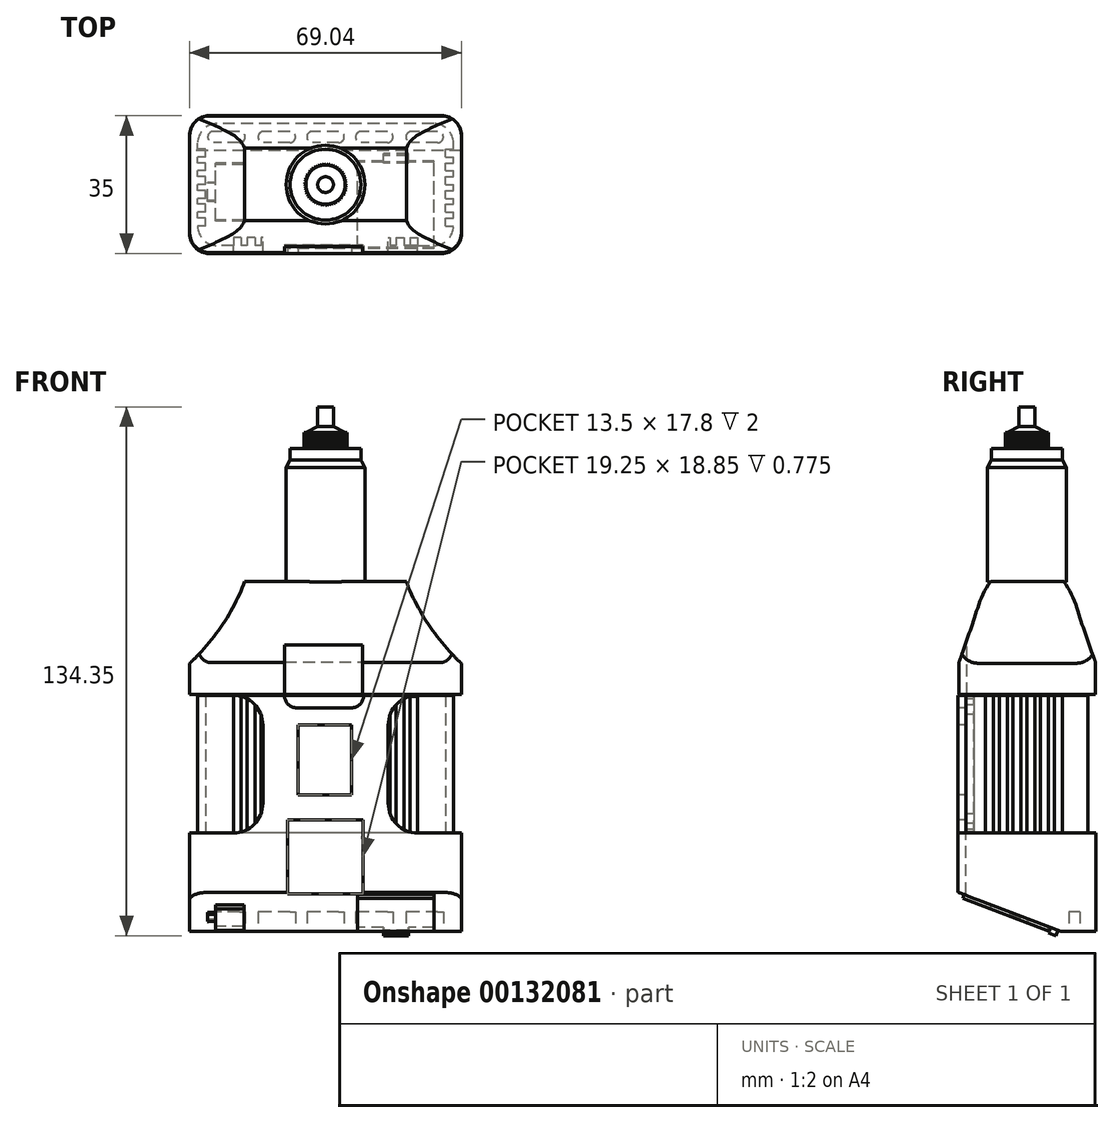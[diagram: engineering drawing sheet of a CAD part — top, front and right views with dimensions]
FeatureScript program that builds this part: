
annotation { "Feature Type Name" : "Feature", "Feature Type Description" : "" }
export const myFeature = defineFeature(function(context is Context, id is Id, definition is map)
    precondition{}
    {
        {
            var Q0;
            Q0=qCreatedBy(makeId("Front.planeOp"),FACE);
            var sketch = newSketch(context, id + "F0", { "sketchPlane" : qUnion([Q0])});
            skLineSegment(sketch, "E0.bottom", {"start": v(32.52, 25.25) * mm, "end": v(-32.53, 25.25) * mm});
            skLineSegment(sketch, "E0.top", {"start": v(32.53, -25.25) * mm, "end": v(-32.52, -25.25) * mm});
            skLineSegment(sketch, "E0.left", {"start": v(32.52, 25.25) * mm, "end": v(32.53, -25.25) * mm});
            skLineSegment(sketch, "E0.right", {"start": v(-32.53, 25.25) * mm, "end": v(-32.52, -25.25) * mm});
            skPoint(sketch, "E0.middle", {"position": v(0, 0) * mm});
            skSolve(sketch);
        }
        {
            var Q0;
            Q0=makeQuery(id+"F0.imprint","IMPRINT",FACE,{"disambiguationData":[TD([[makeQuery(id+"F0.imprint","IMPRINT",EDGE,{"derivedFrom":sQuery(id+"F0.wireOp",EDGE,"E0.bottom")}),1.0]])]});
            extrude(context, id + "F1", {"entities" : qUnion([Q0]), "endBound" : BoundingType.SYMMETRIC, "depth" : 31 * mm});
        }
        {
            var Q0;
            Q0=makeQuery(id+"F1.opExtrude","CAP_FACE",FACE,{"disambiguationData":[OSD([sQuery(id+"F0.wireOp",EDGE,"E0.bottom"),sQuery(id+"F0.wireOp",EDGE,"E0.top"),sQuery(id+"F0.wireOp",EDGE,"E0.left"),sQuery(id+"F0.wireOp",EDGE,"E0.right")])],"isStart":false});
            var sketch = newSketch(context, id + "F2", { "sketchPlane" : qUnion([Q0])});
            skLineSegment(sketch, "E1", {"start": v(-32.52, -9.75) * mm, "end": v(-23.43, -9.75) * mm});
            skLineSegment(sketch, "E2", {"start": v(-32.52, -25.25) * mm, "end": v(32.53, -25.25) * mm});
            skLineSegment(sketch, "E3", {"start": v(-15.93, 17.75) * mm, "end": v(-15.92, -2.25) * mm});
            skLineSegment(sketch, "E4", {"start": v(15.92, 17.75) * mm, "end": v(15.92, -2.25) * mm});
            skLineSegment(sketch, "E5", {"start": v(-32.52, -9.75) * mm, "end": v(-32.52, -25.25) * mm});
            skLineSegment(sketch, "E6", {"start": v(32.53, -9.75) * mm, "end": v(32.53, -25.25) * mm});
            skLineSegment(sketch, "E7.trimOffspring", {"start": v(23.43, -9.75) * mm, "end": v(32.53, -9.75) * mm});
            skArc(sketch, "E8", {"start": v(-23.43, -9.75) * mm, "mid": v(-18.12, -7.55) * mm, "end": v(-15.92, -2.25) * mm});
            skArc(sketch, "E9", {"start": v(15.92, -2.25) * mm, "mid": v(18.12, -7.55) * mm, "end": v(23.43, -9.75) * mm});
            skPoint(sketch, "E10.orphan", {"position": v(-15.93, 25.25) * mm});
            skPoint(sketch, "E11.start.orphan", {"position": v(-23.43, 25.25) * mm});
            skArc(sketch, "E12", {"start": v(-15.93, 17.75) * mm, "mid": v(-18.12, 23.05) * mm, "end": v(-23.43, 25.25) * mm});
            skPoint(sketch, "E13.orphan", {"position": v(15.92, 25.25) * mm});
            skPoint(sketch, "E14.trimOffspring.end.orphan", {"position": v(32.52, 17.75) * mm});
            skLineSegment(sketch, "E15.trimOffspring", {"start": v(15.92, 25.25) * mm, "end": v(-15.93, 25.25) * mm});
            skPoint(sketch, "E16.trimOffspring.end.orphan", {"position": v(32.53, -2.25) * mm});
            skArc(sketch, "E17", {"start": v(23.42, 25.25) * mm, "mid": v(18.12, 23.05) * mm, "end": v(15.92, 17.75) * mm});
            skLineSegment(sketch, "E18", {"start": v(-23.43, 25.25) * mm, "end": v(-15.93, 25.25) * mm});
            skLineSegment(sketch, "E19", {"start": v(15.92, 25.25) * mm, "end": v(23.42, 25.25) * mm});
            skPoint(sketch, "E20.start.orphan", {"position": v(32.52, 25.25) * mm});
            skSolve(sketch);
        }
        {
            var Q0;
            Q0 = qSketchRegion(id + "F2", true);
            extrude(context, id + "F3", {"entities" : qUnion([Q0]), "operationType" : NewBodyOperationType.ADD, "depth" : 2 * mm});
        }
        {
            var Q0;
            Q0=makeQuery(id+"F3.opExtrude","CAP_FACE",FACE,{"disambiguationData":[OSD([sQuery(id+"F2.wireOp",EDGE,"E1"),sQuery(id+"F2.wireOp",EDGE,"E2"),sQuery(id+"F2.wireOp",EDGE,"E3"),sQuery(id+"F2.wireOp",EDGE,"E4"),sQuery(id+"F2.wireOp",EDGE,"E5"),sQuery(id+"F2.wireOp",EDGE,"E6"),sQuery(id+"F2.wireOp",EDGE,"E7.trimOffspring"),sQuery(id+"F2.wireOp",EDGE,"E8"),sQuery(id+"F2.wireOp",EDGE,"E9"),sQuery(id+"F2.wireOp",EDGE,"E12"),sQuery(id+"F2.wireOp",EDGE,"E15.trimOffspring"),sQuery(id+"F2.wireOp",EDGE,"E17"),sQuery(id+"F2.wireOp",EDGE,"E18"),sQuery(id+"F2.wireOp",EDGE,"E19")])],"isStart":false});
            var sketch = newSketch(context, id + "F4", { "sketchPlane" : qUnion([Q0])});
            skLineSegment(sketch, "E21", {"start": v(-15.93, 17.75) * mm, "end": v(15.92, 17.75) * mm, "construction": true});
            skLineSegment(sketch, "E22.bottom", {"start": v(-6.93, 17.75) * mm, "end": v(6.57, 17.75) * mm});
            skLineSegment(sketch, "E22.top", {"start": v(-6.93, -0.05) * mm, "end": v(6.57, -0.05) * mm});
            skLineSegment(sketch, "E22.left", {"start": v(-6.93, 17.75) * mm, "end": v(-6.93, -0.05) * mm});
            skLineSegment(sketch, "E22.right", {"start": v(6.57, 17.75) * mm, "end": v(6.57, -0.05) * mm});
            skLineSegment(sketch, "E23", {"start": v(-7.26, 22.05) * mm, "end": v(6.5, 22.05) * mm});
            skPoint(sketch, "E24.start.orphan", {"position": v(9.39, 25.25) * mm});
            skArc(sketch, "E25", {"start": v(6.5, 22.05) * mm, "mid": v(8.76, 22.99) * mm, "end": v(9.7, 25.25) * mm});
            skPoint(sketch, "E26.orphan", {"position": v(-10.85, 25.25) * mm});
            skArc(sketch, "E27", {"start": v(-7.26, 22.05) * mm, "mid": v(-9.52, 22.99) * mm, "end": v(-10.46, 25.25) * mm});
            skLineSegment(sketch, "E28", {"start": v(-9.7, -25.25) * mm, "end": v(-9.7, -6.4) * mm});
            skLineSegment(sketch, "E29", {"start": v(-9.7, -6.4) * mm, "end": v(9.56, -6.4) * mm});
            skLineSegment(sketch, "E30", {"start": v(9.56, -6.4) * mm, "end": v(9.56, -25.25) * mm});
            skSolve(sketch);
        }
        {
            var Q0;
            Q0=makeQuery(id+"F3.boolean.opBoolean","MERGE",FACE,{"derivedFrom":[makeQuery(id+"F1.opExtrude","SWEPT_FACE",FACE,{"disambiguationData":[OSD([sQuery(id+"F0.wireOp",EDGE,"E0.top")])]}),makeQuery(id+"F3.opExtrude","SWEPT_FACE",FACE,{"disambiguationData":[OSD([sQuery(id+"F2.wireOp",EDGE,"E2")])]})]});
            var sketch = newSketch(context, id + "F5", { "sketchPlane" : qUnion([Q0])});
            skLineSegment(sketch, "E31.bottom", {"start": v(-32.52, 17.5) * mm, "end": v(32.53, 17.5) * mm});
            skLineSegment(sketch, "E31.top", {"start": v(-32.52, -15.5) * mm, "end": v(32.53, -15.5) * mm});
            skLineSegment(sketch, "E31.left", {"start": v(-32.52, 17.5) * mm, "end": v(-32.52, -15.5) * mm});
            skLineSegment(sketch, "E31.right", {"start": v(32.53, 17.5) * mm, "end": v(32.53, -15.5) * mm});
            skSolve(sketch);
        }
        {
            var Q0;
            Q0 = qSketchRegion(id + "F5", true);
            extrude(context, id + "F6", {"entities" : qUnion([Q0]), "operationType" : NewBodyOperationType.ADD, "depth" : 9.5 * mm});
        }
        {
            var Q0;
            Q0=makeQuery(id+"F6.boolean.opBoolean","MERGE",FACE,{"derivedFrom":[makeQuery(id+"F3.boolean.opBoolean","MERGE",FACE,{"derivedFrom":[makeQuery(id+"F1.opExtrude","SWEPT_FACE",FACE,{"disambiguationData":[OSD([sQuery(id+"F0.wireOp",EDGE,"E0.right")])]}),makeQuery(id+"F3.opExtrude","SWEPT_FACE",FACE,{"disambiguationData":[OSD([sQuery(id+"F2.wireOp",EDGE,"E5")])]})]}),makeQuery(id+"F6.opExtrude","SWEPT_FACE",FACE,{"disambiguationData":[OSD([sQuery(id+"F5.wireOp",EDGE,"E31.left")])]})]});
            var sketch = newSketch(context, id + "F7", { "sketchPlane" : qUnion([Q0])});
            skLineSegment(sketch, "E32", {"start": v(-8.68, -34.75) * mm, "end": v(17.5, -24.78) * mm});
            skLineSegment(sketch, "E33", {"start": v(17.5, -24.78) * mm, "end": v(17.5, -34.75) * mm});
            skLineSegment(sketch, "E34", {"start": v(17.5, -34.75) * mm, "end": v(-8.68, -34.75) * mm});
            skSolve(sketch);
        }
        {
            var Q0;
            Q0 = qSketchRegion(id + "F7", true);
            extrude(context, id + "F8", {"entities" : qUnion([Q0]), "operationType" : NewBodyOperationType.REMOVE, "endBound" : BoundingType.THROUGH_ALL, "oppositeDirection" : true, "depth" : 25 * mm});
        }
        {
            var Q0;
            Q0 = qSketchRegion(id + "F4", true);
            extrude(context, id + "F9", {"entities" : qUnion([Q0]), "operationType" : NewBodyOperationType.REMOVE, "oppositeDirection" : true, "depth" : 2 * mm});
        }
        {
            var Q0;
            {var subQ0=sQuery(id+"F4.wireOp",EDGE,"E28");Q0=makeQuery(id+"F4.imprint","IMPRINT",FACE,{"disambiguationData":[TD([[makeQuery(id+"F4.imprint","IMPRINT",EDGE,{"derivedFrom":subQ0}),-1.0]])]});}
            extrude(context, id + "F10", {"entities" : qUnion([Q0]), "operationType" : NewBodyOperationType.REMOVE, "oppositeDirection" : true, "depth" : 2 * mm});
        }
        {
            var Q0;
            Q0=makeQuery(id+"F4.imprint","IMPRINT",FACE,{"disambiguationData":[TD([[makeQuery(id+"F4.imprint","IMPRINT",EDGE,{"derivedFrom":sQuery(id+"F4.wireOp",EDGE,"E23")}),1.0]])]});
            extrude(context, id + "F11", {"entities" : qUnion([Q0]), "operationType" : NewBodyOperationType.REMOVE, "oppositeDirection" : true, "depth" : 2 * mm});
        }
        {
            var Q0;
            Q0=makeQuery(id+"F6.opExtrude","CAP_FACE",FACE,{"disambiguationData":[OSD([sQuery(id+"F5.wireOp",EDGE,"E31.bottom"),sQuery(id+"F5.wireOp",EDGE,"E31.top"),sQuery(id+"F5.wireOp",EDGE,"E31.left"),sQuery(id+"F5.wireOp",EDGE,"E31.right")])],"isStart":false});
            var sketch = newSketch(context, id + "F12", { "sketchPlane" : qUnion([Q0])});
            skLineSegment(sketch, "E35.bottom", {"start": v(-21.85, -10.66) * mm, "end": v(-28.5, -10.66) * mm});
            skLineSegment(sketch, "E35.top", {"start": v(-21.85, -13.51) * mm, "end": v(-28.5, -13.51) * mm});
            skPoint(sketch, "E35.middle", {"position": v(-25.17, -12.1) * mm});
            skLineSegment(sketch, "E36.bottom", {"start": v(-9.07, -10.66) * mm, "end": v(-15.71, -10.66) * mm});
            skLineSegment(sketch, "E36.top", {"start": v(-9.07, -13.52) * mm, "end": v(-15.71, -13.52) * mm});
            skPoint(sketch, "E36.middle", {"position": v(-12.39, -12.09) * mm});
            skLineSegment(sketch, "E37.bottom", {"start": v(3.32, -10.66) * mm, "end": v(-3.32, -10.66) * mm});
            skLineSegment(sketch, "E37.top", {"start": v(3.33, -13.52) * mm, "end": v(-3.32, -13.52) * mm});
            skPoint(sketch, "E37.middle", {"position": v(0, -12.1) * mm});
            skLineSegment(sketch, "E38.bottom", {"start": v(15.71, -10.67) * mm, "end": v(9.06, -10.67) * mm});
            skLineSegment(sketch, "E38.top", {"start": v(15.71, -13.51) * mm, "end": v(9.06, -13.51) * mm});
            skPoint(sketch, "E38.middle", {"position": v(12.39, -12.09) * mm});
            skLineSegment(sketch, "E39.bottom", {"start": v(28.5, -10.66) * mm, "end": v(21.85, -10.66) * mm});
            skLineSegment(sketch, "E39.top", {"start": v(28.5, -13.51) * mm, "end": v(21.85, -13.51) * mm});
            skPoint(sketch, "E39.middle", {"position": v(25.18, -12.09) * mm});
            skArc(sketch, "E40", {"start": v(-28.5, -10.66) * mm, "mid": v(-29.92, -12.09) * mm, "end": v(-28.5, -13.51) * mm});
            skArc(sketch, "E41", {"start": v(-21.85, -10.67) * mm, "mid": v(-20.42, -12.1) * mm, "end": v(-21.85, -13.51) * mm});
            skArc(sketch, "E42", {"start": v(28.5, -10.66) * mm, "mid": v(29.93, -12.09) * mm, "end": v(28.5, -13.51) * mm});
            skArc(sketch, "E43", {"start": v(21.85, -10.66) * mm, "mid": v(20.43, -12.09) * mm, "end": v(21.85, -13.51) * mm});
            skArc(sketch, "E44", {"start": v(-3.33, -13.52) * mm, "mid": v(-4.75, -12.1) * mm, "end": v(-3.32, -10.66) * mm});
            skArc(sketch, "E45", {"start": v(3.32, -10.67) * mm, "mid": v(4.75, -12.1) * mm, "end": v(3.33, -13.52) * mm});
            skArc(sketch, "E46", {"start": v(-9.07, -10.66) * mm, "mid": v(-7.64, -12.09) * mm, "end": v(-9.07, -13.52) * mm});
            skArc(sketch, "E47", {"start": v(-15.71, -10.66) * mm, "mid": v(-17.14, -12.09) * mm, "end": v(-15.71, -13.52) * mm});
            skArc(sketch, "E48", {"start": v(15.71, -10.67) * mm, "mid": v(17.14, -12.1) * mm, "end": v(15.71, -13.51) * mm});
            skArc(sketch, "E49", {"start": v(9.06, -10.67) * mm, "mid": v(7.64, -12.1) * mm, "end": v(9.06, -13.51) * mm});
            skSolve(sketch);
        }
        {
            var Q0;
            Q0 = qSketchRegion(id + "F12", true);
            extrude(context, id + "F13", {"entities" : qUnion([Q0]), "operationType" : NewBodyOperationType.REMOVE, "oppositeDirection" : true, "depth" : 5 * mm});
        }
        {
            var Q0;
            Q0=makeQuery(id+"F6.boolean.opBoolean","MERGE",FACE,{"derivedFrom":[makeQuery(id+"F3.boolean.opBoolean","MERGE",FACE,{"derivedFrom":[makeQuery(id+"F1.opExtrude","SWEPT_FACE",FACE,{"disambiguationData":[OSD([sQuery(id+"F0.wireOp",EDGE,"E0.right")])]}),makeQuery(id+"F3.opExtrude","SWEPT_FACE",FACE,{"disambiguationData":[OSD([sQuery(id+"F2.wireOp",EDGE,"E5")])]})]}),makeQuery(id+"F6.opExtrude","SWEPT_FACE",FACE,{"disambiguationData":[OSD([sQuery(id+"F5.wireOp",EDGE,"E31.left")])]})]});
            var sketch = newSketch(context, id + "F14", { "sketchPlane" : qUnion([Q0])});
            skLineSegment(sketch, "E50", {"start": v(17.5, -9.75) * mm, "end": v(-15.5, -9.75) * mm});
            skLineSegment(sketch, "E51", {"start": v(-15.5, -9.75) * mm, "end": v(-15.5, -34.75) * mm});
            skLineSegment(sketch, "E52", {"start": v(-15.5, -34.75) * mm, "end": v(-8.68, -34.75) * mm});
            skLineSegment(sketch, "E53", {"start": v(-8.68, -34.75) * mm, "end": v(17.5, -24.78) * mm});
            skLineSegment(sketch, "E54", {"start": v(17.5, -24.78) * mm, "end": v(17.5, -9.75) * mm});
            skSolve(sketch);
        }
        {
            var Q0;
            Q0 = qSketchRegion(id + "F14", true);
            extrude(context, id + "F15", {"entities" : qUnion([Q0]), "operationType" : NewBodyOperationType.ADD, "depth" : 2 * mm});
        }
        {
            var Q0;
            Q0=makeQuery(id+"F6.boolean.opBoolean","MERGE",FACE,{"derivedFrom":[makeQuery(id+"F3.boolean.opBoolean","MERGE",FACE,{"derivedFrom":[makeQuery(id+"F1.opExtrude","SWEPT_FACE",FACE,{"disambiguationData":[OSD([sQuery(id+"F0.wireOp",EDGE,"E0.left")])]}),makeQuery(id+"F3.opExtrude","SWEPT_FACE",FACE,{"disambiguationData":[OSD([sQuery(id+"F2.wireOp",EDGE,"E6")])]})]}),makeQuery(id+"F6.opExtrude","SWEPT_FACE",FACE,{"disambiguationData":[OSD([sQuery(id+"F5.wireOp",EDGE,"E31.right")])]})]});
            var sketch = newSketch(context, id + "F16", { "sketchPlane" : qUnion([Q0])});
            skLineSegment(sketch, "E55", {"start": v(-17.5, -9.75) * mm, "end": v(15.5, -9.75) * mm});
            skLineSegment(sketch, "E56", {"start": v(15.5, -9.75) * mm, "end": v(15.5, -34.75) * mm});
            skLineSegment(sketch, "E57", {"start": v(15.5, -34.75) * mm, "end": v(8.68, -34.75) * mm});
            skLineSegment(sketch, "E58", {"start": v(8.68, -34.75) * mm, "end": v(-17.5, -24.78) * mm});
            skLineSegment(sketch, "E59", {"start": v(-17.5, -24.78) * mm, "end": v(-17.5, -9.75) * mm});
            skSolve(sketch);
        }
        {
            var Q0;
            Q0 = qSketchRegion(id + "F16", true);
            extrude(context, id + "F17", {"entities" : qUnion([Q0]), "operationType" : NewBodyOperationType.ADD, "depth" : 2 * mm});
        }
        {
            var Q0;
            Q0=makeQuery(id+"F17.boolean.opBoolean","MERGE",FACE,{"derivedFrom":[makeQuery(id+"F15.boolean.opBoolean","MERGE",FACE,{"derivedFrom":[makeQuery(id+"F6.boolean.opBoolean","MERGE",FACE,{"derivedFrom":[makeQuery(id+"F1.opExtrude","CAP_FACE",FACE,{"disambiguationData":[OSD([sQuery(id+"F0.wireOp",EDGE,"E0.bottom"),sQuery(id+"F0.wireOp",EDGE,"E0.top"),sQuery(id+"F0.wireOp",EDGE,"E0.left"),sQuery(id+"F0.wireOp",EDGE,"E0.right")])],"isStart":true}),makeQuery(id+"F6.opExtrude","SWEPT_FACE",FACE,{"disambiguationData":[OSD([sQuery(id+"F5.wireOp",EDGE,"E31.top")])]})]}),makeQuery(id+"F15.opExtrude","SWEPT_FACE",FACE,{"disambiguationData":[OSD([sQuery(id+"F14.wireOp",EDGE,"E51")])]})]}),makeQuery(id+"F17.opExtrude","SWEPT_FACE",FACE,{"disambiguationData":[OSD([sQuery(id+"F16.wireOp",EDGE,"E56")])]})]});
            var sketch = newSketch(context, id + "F18", { "sketchPlane" : qUnion([Q0])});
            skLineSegment(sketch, "E60", {"start": v(-34.53, -9.75) * mm, "end": v(34.52, -9.75) * mm});
            skLineSegment(sketch, "E61", {"start": v(-34.53, -9.75) * mm, "end": v(-34.53, -34.75) * mm});
            skLineSegment(sketch, "E62", {"start": v(-34.53, -34.75) * mm, "end": v(34.52, -34.75) * mm});
            skLineSegment(sketch, "E63", {"start": v(34.52, -34.75) * mm, "end": v(34.52, -9.75) * mm});
            skSolve(sketch);
        }
        {
            var Q0;
            Q0 = qSketchRegion(id + "F18", true);
            extrude(context, id + "F19", {"entities" : qUnion([Q0]), "operationType" : NewBodyOperationType.ADD, "depth" : 2 * mm});
        }
        {
            var Q0;
            Q0=makeQuery(id+"F17.boolean.opBoolean","MERGE",FACE,{"derivedFrom":[makeQuery(id+"F15.boolean.opBoolean","MERGE",FACE,{"derivedFrom":[makeQuery(id+"F8.boolean.opBoolean","COPY",FACE,{"derivedFrom":makeQuery(id+"F8.opExtrude","SWEPT_FACE",FACE,{"disambiguationData":[OSD([sQuery(id+"F7.wireOp",EDGE,"E32")])]})}),makeQuery(id+"F15.opExtrude","SWEPT_FACE",FACE,{"disambiguationData":[OSD([sQuery(id+"F14.wireOp",EDGE,"E53")])]})]}),makeQuery(id+"F17.opExtrude","SWEPT_FACE",FACE,{"disambiguationData":[OSD([sQuery(id+"F16.wireOp",EDGE,"E58")])]})]});
            var sketch = newSketch(context, id + "F20", { "sketchPlane" : qUnion([Q0])});
            skLineSegment(sketch, "E64.bottom", {"start": v(27.6, 5.87) * mm, "end": v(8.1, 5.87) * mm});
            skLineSegment(sketch, "E64.top", {"start": v(27.6, -17.63) * mm, "end": v(8.1, -17.63) * mm});
            skLineSegment(sketch, "E64.left", {"start": v(27.6, 5.87) * mm, "end": v(27.6, -17.63) * mm});
            skLineSegment(sketch, "E64.right", {"start": v(8.1, 5.87) * mm, "end": v(8.1, -17.63) * mm});
            skPoint(sketch, "E64.middle", {"position": v(17.85, -5.88) * mm});
            skLineSegment(sketch, "E65.bottom", {"start": v(-20.69, -1.6) * mm, "end": v(-27.99, -1.6) * mm});
            skLineSegment(sketch, "E65.top", {"start": v(-20.69, -17) * mm, "end": v(-27.99, -17) * mm});
            skLineSegment(sketch, "E65.left", {"start": v(-20.69, -1.6) * mm, "end": v(-20.69, -17) * mm});
            skLineSegment(sketch, "E65.right", {"start": v(-27.99, -1.6) * mm, "end": v(-27.99, -17) * mm});
            skPoint(sketch, "E65.middle", {"position": v(-24.34, -9.3) * mm});
            skLineSegment(sketch, "E66.bottom", {"start": v(-27.99, -6.8) * mm, "end": v(-29.99, -6.8) * mm});
            skLineSegment(sketch, "E66.top", {"start": v(-27.99, -11.8) * mm, "end": v(-29.99, -11.8) * mm});
            skLineSegment(sketch, "E66.left", {"start": v(-27.99, -6.8) * mm, "end": v(-27.99, -11.8) * mm});
            skLineSegment(sketch, "E66.right", {"start": v(-29.99, -6.8) * mm, "end": v(-29.99, -11.8) * mm});
            skPoint(sketch, "E66.middle", {"position": v(-28.99, -9.3) * mm});
            skPoint(sketch, "E66.middle.positionSnap0", {"position": v(-27.99, -9.3) * mm});
            skPoint(sketch, "E66.centerSnap0", {"position": v(-27.99, -9.3) * mm});
            skLineSegment(sketch, "E67.bottom", {"start": v(21.03, -17.63) * mm, "end": v(14.68, -17.63) * mm});
            skLineSegment(sketch, "E67.top", {"start": v(21.03, -19.63) * mm, "end": v(14.68, -19.63) * mm});
            skLineSegment(sketch, "E67.left", {"start": v(21.03, -17.63) * mm, "end": v(21.03, -19.63) * mm});
            skLineSegment(sketch, "E67.right", {"start": v(14.68, -17.63) * mm, "end": v(14.68, -19.63) * mm});
            skPoint(sketch, "E67.middle", {"position": v(17.85, -18.63) * mm});
            skPoint(sketch, "E67.middle.positionSnap0", {"position": v(17.85, -17.63) * mm});
            skPoint(sketch, "E67.centerSnap0", {"position": v(17.85, -17.63) * mm});
            skSolve(sketch);
        }
        {
            var Q0;
            Q0=qCreatedBy(makeId("Right.planeOp"),FACE);
            cPlane(context, id + "F21", {"entities" : qUnion([Q0]), "cplaneType" : CPlaneType.OFFSET, "offset" : 34.5 * mm, "width" : 150 * mm, "height" : 150 * mm});
        }
        {
            var Q0;
            Q0=qCreatedBy(id+"F21.planeOp",FACE);
            var sketch = newSketch(context, id + "F22", { "sketchPlane" : qUnion([Q0])});
            skLineSegment(sketch, "E68.bottom", {"start": v(-17.27, 25.48) * mm, "end": v(17.46, 25.48) * mm});
            skLineSegment(sketch, "E68.top", {"start": v(-17.27, 58.58) * mm, "end": v(17.46, 58.58) * mm});
            skLineSegment(sketch, "E68.left", {"start": v(-17.27, 25.48) * mm, "end": v(-17.27, 58.58) * mm});
            skLineSegment(sketch, "E68.right", {"start": v(17.46, 25.48) * mm, "end": v(17.46, 58.58) * mm});
            skSolve(sketch);
        }
        {
            var Q0;
            Q0 = qSketchRegion(id + "F22", true);
            extrude(context, id + "F23", {"entities" : qUnion([Q0]), "oppositeDirection" : true, "depth" : 69 * mm});
        }
        {
            var Q0;
            Q0=makeQuery(id+"F23.opExtrude","SWEPT_FACE",FACE,{"disambiguationData":[OSD([sQuery(id+"F22.wireOp",EDGE,"E68.left")])]});
            var sketch = newSketch(context, id + "F24", { "sketchPlane" : qUnion([Q0])});
            skLineSegment(sketch, "E69", {"start": v(-34.5, 25.48) * mm, "end": v(-34.5, 33.38) * mm});
            skLineSegment(sketch, "E70", {"start": v(34.5, 25.48) * mm, "end": v(34.5, 33.38) * mm});
            skArc(sketch, "E71", {"start": v(-34.5, 33.38) * mm, "mid": v(-25.06, 44.94) * mm, "end": v(-19, 58.58) * mm});
            skArc(sketch, "E72", {"start": v(19, 58.58) * mm, "mid": v(25.06, 44.94) * mm, "end": v(34.5, 33.38) * mm});
            skLineSegment(sketch, "E73", {"start": v(-19, 58.58) * mm, "end": v(-34.5, 58.58) * mm});
            skLineSegment(sketch, "E74", {"start": v(-34.5, 58.58) * mm, "end": v(-34.5, 33.38) * mm});
            skLineSegment(sketch, "E75", {"start": v(19, 58.58) * mm, "end": v(34.5, 58.58) * mm});
            skLineSegment(sketch, "E76", {"start": v(34.5, 58.58) * mm, "end": v(34.5, 33.38) * mm});
            skSolve(sketch);
        }
        {
            var Q0;
            Q0 = qSketchRegion(id + "F24", true);
            extrude(context, id + "F25", {"entities" : qUnion([Q0]), "operationType" : NewBodyOperationType.REMOVE, "endBound" : BoundingType.THROUGH_ALL, "oppositeDirection" : true, "depth" : 25 * mm});
        }
        {
            var Q0;
            Q0=qCreatedBy(makeId("Right.planeOp"),FACE);
            cPlane(context, id + "F26", {"entities" : qUnion([Q0]), "cplaneType" : CPlaneType.OFFSET, "offset" : 34.5 * mm, "oppositeDirection" : true, "width" : 150 * mm, "height" : 150 * mm});
        }
        {
            var Q0;
            Q0=qCreatedBy(id+"F26.planeOp",FACE);
            var sketch = newSketch(context, id + "F27", { "sketchPlane" : qUnion([Q0])});
            skPoint(sketch, "E77", {"position": v(0, 58.6) * mm});
            skPoint(sketch, "E78", {"position": v(-17.3, 33.51) * mm});
            skPoint(sketch, "E79", {"position": v(17.49, 33.51) * mm});
            skPoint(sketch, "E80", {"position": v(-9.07, 54.2) * mm});
            skPoint(sketch, "E81", {"position": v(-13.46, 44.5) * mm});
            skPoint(sketch, "E82", {"position": v(13.64, 44.5) * mm});
            skPoint(sketch, "E83", {"position": v(9.26, 54.2) * mm});
            skFitSpline(sketch, "E84", {"points": [v(17.49, 33.51) * mm, v(13.64, 44.5) * mm, v(9.26, 54.2) * mm, v(0, 58.6) * mm, v(-9.07, 54.2) * mm, v(-13.46, 44.5) * mm, v(-17.3, 33.51) * mm], "startDerivative": vector(-23.18, 63.45) * mm, "endDerivative": vector(-23.08, -63.46) * mm});
            skLineSegment(sketch, "E85", {"start": v(17.49, 33.51) * mm, "end": v(17.49, 58.79) * mm});
            skLineSegment(sketch, "E86", {"start": v(17.49, 58.79) * mm, "end": v(-17.49, 58.6) * mm});
            skLineSegment(sketch, "E87", {"start": v(-17.49, 58.6) * mm, "end": v(-17.3, 33.51) * mm});
            skSolve(sketch);
        }
        {
            var Q0;
            Q0 = qSketchRegion(id + "F27", true);
            extrude(context, id + "F28", {"entities" : qUnion([Q0]), "operationType" : NewBodyOperationType.REMOVE, "endBound" : BoundingType.THROUGH_ALL, "depth" : 25 * mm});
        }
        {
            var Q0;
            Q0=makeQuery(id+"F23.opExtrude","SWEPT_FACE",FACE,{"disambiguationData":[OSD([sQuery(id+"F22.wireOp",EDGE,"E68.left")])]});
            var sketch = newSketch(context, id + "F29", { "sketchPlane" : qUnion([Q0])});
            skLineSegment(sketch, "E88.bottom", {"start": v(-10.4, 25.48) * mm, "end": v(9.39, 25.48) * mm});
            skLineSegment(sketch, "E88.top", {"start": v(-10.4, 37.98) * mm, "end": v(9.39, 37.98) * mm});
            skLineSegment(sketch, "E88.left", {"start": v(-10.4, 25.48) * mm, "end": v(-10.4, 37.98) * mm});
            skLineSegment(sketch, "E88.right", {"start": v(9.39, 25.48) * mm, "end": v(9.39, 37.98) * mm});
            skSolve(sketch);
        }
        {
            var Q0;
            Q0 = qSketchRegion(id + "F29", true);
            extrude(context, id + "F30", {"entities" : qUnion([Q0]), "operationType" : NewBodyOperationType.REMOVE, "oppositeDirection" : true, "depth" : 2 * mm});
        }
        {
            var Q0;
            Q0 = qSketchRegion(id + "F20", true);
            extrude(context, id + "F31", {"entities" : qUnion([Q0]), "operationType" : NewBodyOperationType.ADD, "depth" : 1 * mm});
        }
        {
            var Q0;
            Q0=makeQuery(id+"F31.opExtrude","CAP_FACE",FACE,{"disambiguationData":[OSD([sQuery(id+"F20.wireOp",EDGE,"E65.bottom"),sQuery(id+"F20.wireOp",EDGE,"E65.top"),sQuery(id+"F20.wireOp",EDGE,"E65.left"),sQuery(id+"F20.wireOp",EDGE,"E65.right"),sQuery(id+"F20.wireOp",EDGE,"E66.bottom"),sQuery(id+"F20.wireOp",EDGE,"E66.top"),sQuery(id+"F20.wireOp",EDGE,"E66.right")])],"isStart":false});
            var sketch = newSketch(context, id + "F32", { "sketchPlane" : qUnion([Q0])});
            skLineSegment(sketch, "E89", {"start": v(-27.99, -6.8) * mm, "end": v(-27.99, -11.8) * mm});
            skLineSegment(sketch, "E90", {"start": v(-27.99, -11.8) * mm, "end": v(-29.99, -11.8) * mm});
            skLineSegment(sketch, "E91", {"start": v(-29.99, -11.8) * mm, "end": v(-29.99, -6.8) * mm});
            skLineSegment(sketch, "E92", {"start": v(-29.99, -6.8) * mm, "end": v(-27.99, -6.8) * mm});
            skSolve(sketch);
        }
        {
            var Q0;
            Q0 = qSketchRegion(id + "F32", true);
            extrude(context, id + "F33", {"entities" : qUnion([Q0]), "operationType" : NewBodyOperationType.REMOVE, "oppositeDirection" : true, "depth" : 0.5 * mm});
        }
        {
            var Q0;
            Q0=makeQuery(id+"F31.opExtrude","CAP_FACE",FACE,{"disambiguationData":[OSD([sQuery(id+"F20.wireOp",EDGE,"E64.bottom"),sQuery(id+"F20.wireOp",EDGE,"E64.top"),sQuery(id+"F20.wireOp",EDGE,"E64.left"),sQuery(id+"F20.wireOp",EDGE,"E64.right"),sQuery(id+"F20.wireOp",EDGE,"E67.top"),sQuery(id+"F20.wireOp",EDGE,"E67.left"),sQuery(id+"F20.wireOp",EDGE,"E67.right")])],"isStart":false});
            var sketch = newSketch(context, id + "F34", { "sketchPlane" : qUnion([Q0])});
            skLineSegment(sketch, "E93", {"start": v(14.68, -17.63) * mm, "end": v(14.68, -19.63) * mm});
            skLineSegment(sketch, "E94", {"start": v(14.68, -19.63) * mm, "end": v(21.03, -19.63) * mm});
            skLineSegment(sketch, "E95", {"start": v(21.03, -19.63) * mm, "end": v(21.03, -17.63) * mm});
            skLineSegment(sketch, "E96", {"start": v(21.03, -17.63) * mm, "end": v(14.68, -17.63) * mm});
            skSolve(sketch);
        }
        {
            var Q0;
            Q0 = qSketchRegion(id + "F34", true);
            extrude(context, id + "F35", {"entities" : qUnion([Q0]), "operationType" : NewBodyOperationType.ADD, "depth" : 0.5 * mm});
        }
        {
            var Q0;
            Q0=qCreatedBy(id+"F21.planeOp",FACE);
            cPlane(context, id + "F36", {"entities" : qUnion([Q0]), "cplaneType" : CPlaneType.OFFSET, "offset" : 34.5 * mm, "oppositeDirection" : true, "width" : 150 * mm, "height" : 150 * mm});
        }
        {
            var Q0;
            Q0=qCreatedBy(id+"F36.planeOp",FACE);
            var sketch = newSketch(context, id + "F37", { "sketchPlane" : qUnion([Q0])});
            skLineSegment(sketch, "E97", {"start": v(0, 56.65) * mm, "end": v(-12.82, 56.65) * mm});
            skLineSegment(sketch, "E98", {"start": v(-12.82, 56.65) * mm, "end": v(0, 56.65) * mm});
            skLineSegment(sketch, "E99", {"start": v(0, 56.65) * mm, "end": v(11.33, 56.65) * mm});
            skArc(sketch, "E100", {"start": v(5.67, 56.65) * mm, "mid": v(-0.37, 58.75) * mm, "end": v(-6.41, 56.65) * mm});
            skSolve(sketch);
        }
        {
            var Q0;
            Q0 = qSketchRegion(id + "F37", true);
            extrude(context, id + "F38", {"entities" : qUnion([Q0]), "operationType" : NewBodyOperationType.REMOVE, "endBound" : BoundingType.THROUGH_ALL, "oppositeDirection" : true, "depth" : 25 * mm});
        }
        {
            var Q0;
            Q0 = qSketchRegion(id + "F37", true);
            extrude(context, id + "F39", {"entities" : qUnion([Q0]), "operationType" : NewBodyOperationType.REMOVE, "endBound" : BoundingType.THROUGH_ALL, "depth" : 25 * mm});
        }
        {
            var Q0;
            Q0=qCreatedBy(id+"F36.planeOp",FACE);
            var sketch = newSketch(context, id + "F40", { "sketchPlane" : qUnion([Q0])});
            skLineSegment(sketch, "E101", {"start": v(5.61, 56.67) * mm, "end": v(0, 58.7) * mm});
            skLineSegment(sketch, "E102", {"start": v(0, 58.7) * mm, "end": v(5.06, 62.93) * mm});
            skLineSegment(sketch, "E103", {"start": v(5.06, 62.93) * mm, "end": v(10.3, 56.67) * mm});
            skLineSegment(sketch, "E104", {"start": v(10.3, 56.67) * mm, "end": v(5.61, 56.67) * mm});
            skSolve(sketch);
        }
        {
            var Q0;
            Q0 = qSketchRegion(id + "F40", true);
            extrude(context, id + "F41", {"entities" : qUnion([Q0]), "operationType" : NewBodyOperationType.REMOVE, "endBound" : BoundingType.THROUGH_ALL, "oppositeDirection" : true, "depth" : 25 * mm});
        }
        {
            var Q0;
            Q0 = qSketchRegion(id + "F40", true);
            extrude(context, id + "F42", {"entities" : qUnion([Q0]), "operationType" : NewBodyOperationType.REMOVE, "endBound" : BoundingType.THROUGH_ALL, "depth" : 25 * mm});
        }
        {
            var Q0;
            Q0=qCreatedBy(id+"F26.planeOp",FACE);
            var sketch = newSketch(context, id + "F43", { "sketchPlane" : qUnion([Q0])});
            skLineSegment(sketch, "E105", {"start": v(9.5, 54.11) * mm, "end": v(-9.29, 54.11) * mm});
            skLineSegment(sketch, "E106", {"start": v(-6.2, 56.8) * mm, "end": v(5.99, 56.8) * mm});
            skLineSegment(sketch, "E107", {"start": v(5.99, 56.8) * mm, "end": v(25.18, 56.8) * mm});
            skLineSegment(sketch, "E108", {"start": v(25.18, 56.8) * mm, "end": v(9.5, 54.11) * mm});
            skLineSegment(sketch, "E109", {"start": v(-9.29, 54.11) * mm, "end": v(-23.94, 54.11) * mm});
            skLineSegment(sketch, "E110", {"start": v(-23.94, 54.11) * mm, "end": v(-6.2, 56.8) * mm});
            skSolve(sketch);
        }
        {
            var Q0;
            Q0 = qSketchRegion(id + "F43", true);
            extrude(context, id + "F44", {"entities" : qUnion([Q0]), "operationType" : NewBodyOperationType.REMOVE, "endBound" : BoundingType.THROUGH_ALL, "depth" : 25 * mm});
        }
        {
            var Q0;
            Q0=qCreatedBy(makeId("Front.planeOp"),FACE);
            var sketch = newSketch(context, id + "F45", { "sketchPlane" : qUnion([Q0])});
            skLineSegment(sketch, "E111", {"start": v(0, 88.2) * mm, "end": v(0, 41.26) * mm, "construction": true});
            skLineSegment(sketch, "E112", {"start": v(0, 54.1) * mm, "end": v(10, 54.1) * mm});
            skLineSegment(sketch, "E113", {"start": v(10, 54.1) * mm, "end": v(10, 83.1) * mm});
            skLineSegment(sketch, "E114", {"start": v(10, 83.1) * mm, "end": v(0, 83.1) * mm});
            skLineSegment(sketch, "E115", {"start": v(0, 83.1) * mm, "end": v(0, 54.1) * mm});
            skSolve(sketch);
        }
        {
            var Q0;
            Q0=makeQuery(id+"F45.imprint","IMPRINT",FACE,{"disambiguationData":[TD([[makeQuery(id+"F45.imprint","IMPRINT",EDGE,{"derivedFrom":sQuery(id+"F45.wireOp",EDGE,"E112")}),1.0]])]});
            var Q1;
            Q1=sQuery(id+"F45.wireOp",EDGE,"E111");
            revolve(context, id + "F46", {"operationType" : NewBodyOperationType.ADD, "entities" : qUnion([Q0]), "axis" : qUnion([Q1]), "revolveType" : RevolveType.FULL});
        }
        {
            var Q0;
            Q0=qCreatedBy(makeId("Top.planeOp"),FACE);
            cPlane(context, id + "F47", {"entities" : qUnion([Q0]), "cplaneType" : CPlaneType.OFFSET, "offset" : 85 * mm, "width" : 150 * mm, "height" : 150 * mm});
        }
        {
            var Q0;
            Q0=qCreatedBy(id+"F47.planeOp",FACE);
            var sketch = newSketch(context, id + "F48", { "sketchPlane" : qUnion([Q0])});
            skCircle(sketch, "E116", {"center": v(0, 0) * mm, "radius": 9 * mm});
            skSolve(sketch);
        }
        {
            var Q1;
            Q1=makeQuery(id+"F46.opRevolve","SWEPT_FACE",FACE,{"disambiguationData":[OSD([sQuery(id+"F45.wireOp",EDGE,"E114")])]});
            var Q2;
            Q2=makeQuery(id+"F48.imprint","IMPRINT",FACE,{"disambiguationData":[TD([[makeQuery(id+"F48.imprint","IMPRINT",EDGE,{"derivedFrom":sQuery(id+"F48.wireOp",EDGE,"E116")}),1.0]])]});
            loft(context, id + "F49", {"sheetProfilesArray" : [{ "sheetProfileEntities" : qUnion([Q1]) }, { "sheetProfileEntities" : qUnion([Q2]) }]});
        }
        {
            var Q0;
            Q0=makeQuery(id+"F49.opLoft","CAP_FACE",FACE,{"disambiguationData":[OSD([makeQuery(id+"F48.imprint","IMPRINT",FACE,{"disambiguationData":[TD([[makeQuery(id+"F48.imprint","IMPRINT",EDGE,{"derivedFrom":sQuery(id+"F48.wireOp",EDGE,"E116")}),1.0]])]})])],"isStart":true});
            var sketch = newSketch(context, id + "F50", { "sketchPlane" : qUnion([Q0])});
            skCircle(sketch, "E117", {"center": v(0, 0) * mm, "radius": 9 * mm});
            skSolve(sketch);
        }
        {
            var Q0;
            Q0 = qSketchRegion(id + "F50", true);
            extrude(context, id + "F51", {"entities" : qUnion([Q0]), "operationType" : NewBodyOperationType.ADD, "depth" : 3 * mm});
        }
        {
            var Q0;
            Q0=makeQuery(id+"F51.opExtrude","CAP_FACE",FACE,{"disambiguationData":[OSD([sQuery(id+"F50.wireOp",EDGE,"E117")])],"isStart":false});
            var sketch = newSketch(context, id + "F52", { "sketchPlane" : qUnion([Q0])});
            skCircle(sketch, "E118", {"center": v(0, 0) * mm, "radius": 5 * mm});
            skCircle(sketch, "E119.cCircle", {"center": v(2.33, -4.42) * mm, "radius": 0.23 * mm, "construction": true});
            skLineSegment(sketch, "E119.0", {"start": v(2.56, -4.3) * mm, "end": v(2.56, -4.81) * mm});
            skLineSegment(sketch, "E119.1", {"start": v(2.56, -4.81) * mm, "end": v(2.1, -4.54) * mm});
            skPoint(sketch, "E119.0.midPoint", {"position": v(2.56, -4.42) * mm});
            skLineSegment(sketch, "E120.1.0", {"start": v(3.4, -3.67) * mm, "end": v(3.5, -4.18) * mm});
            skLineSegment(sketch, "E120.2.0", {"start": v(4.08, -2.88) * mm, "end": v(4.3, -3.36) * mm});
            skLineSegment(sketch, "E121.2.3.0", {"start": v(4.6, -1.97) * mm, "end": v(4.9, -2.39) * mm});
            skLineSegment(sketch, "E121.2.4.0", {"start": v(4.9, -0.97) * mm, "end": v(5.29, -1.32) * mm});
            skLineSegment(sketch, "E121.2.5.0", {"start": v(5, 0.07) * mm, "end": v(5.45, -0.2) * mm});
            skLineSegment(sketch, "E121.2.6.0", {"start": v(4.88, 1.1) * mm, "end": v(5.37, 0.95) * mm});
            skLineSegment(sketch, "E121.2.7.0", {"start": v(4.54, 2.1) * mm, "end": v(5.05, 2.04) * mm});
            skLineSegment(sketch, "E121.2.8.0", {"start": v(4, 3) * mm, "end": v(4.52, 3.05) * mm});
            skLineSegment(sketch, "E121.2.9.0", {"start": v(3.3, 3.76) * mm, "end": v(3.79, 3.92) * mm});
            skLineSegment(sketch, "E121.2.10.0", {"start": v(2.44, 4.36) * mm, "end": v(2.89, 4.62) * mm});
            skLineSegment(sketch, "E121.2.11.0", {"start": v(1.48, 4.78) * mm, "end": v(1.86, 5.12) * mm});
            skLineSegment(sketch, "E121.2.12.0", {"start": v(0.46, 4.98) * mm, "end": v(0.76, 5.4) * mm});
            skLineSegment(sketch, "E121.2.13.0", {"start": v(-0.6, 4.97) * mm, "end": v(-0.38, 5.44) * mm});
            skLineSegment(sketch, "E121.2.14.0", {"start": v(-1.6, 4.73) * mm, "end": v(-1.5, 5.24) * mm});
            skLineSegment(sketch, "E121.2.15.0", {"start": v(-2.56, 4.3) * mm, "end": v(-2.56, 4.81) * mm});
            skLineSegment(sketch, "E121.2.16.0", {"start": v(-3.4, 3.67) * mm, "end": v(-3.5, 4.18) * mm});
            skLineSegment(sketch, "E121.2.17.0", {"start": v(-4.08, 2.88) * mm, "end": v(-4.3, 3.36) * mm});
            skLineSegment(sketch, "E121.2.18.0", {"start": v(-4.6, 1.97) * mm, "end": v(-4.9, 2.39) * mm});
            skLineSegment(sketch, "E121.2.19.0", {"start": v(-4.9, 0.97) * mm, "end": v(-5.29, 1.32) * mm});
            skLineSegment(sketch, "E121.2.20.0", {"start": v(-5, -0.07) * mm, "end": v(-5.45, 0.2) * mm});
            skLineSegment(sketch, "E121.2.21.0", {"start": v(-4.88, -1.1) * mm, "end": v(-5.37, -0.95) * mm});
            skLineSegment(sketch, "E121.2.22.0", {"start": v(-4.54, -2.1) * mm, "end": v(-5.05, -2.04) * mm});
            skLineSegment(sketch, "E121.2.23.0", {"start": v(-4, -3) * mm, "end": v(-4.52, -3.05) * mm});
            skLineSegment(sketch, "E121.2.24.0", {"start": v(-3.3, -3.76) * mm, "end": v(-3.79, -3.92) * mm});
            skLineSegment(sketch, "E121.2.25.0", {"start": v(-2.44, -4.36) * mm, "end": v(-2.89, -4.62) * mm});
            skLineSegment(sketch, "E121.2.26.0", {"start": v(-1.48, -4.78) * mm, "end": v(-1.86, -5.12) * mm});
            skLineSegment(sketch, "E121.2.27.0", {"start": v(-0.46, -4.98) * mm, "end": v(-0.76, -5.4) * mm});
            skLineSegment(sketch, "E121.2.28.0", {"start": v(0.6, -4.97) * mm, "end": v(0.38, -5.44) * mm});
            skLineSegment(sketch, "E121.2.29.0", {"start": v(1.6, -4.73) * mm, "end": v(1.5, -5.24) * mm});
            skLineSegment(sketch, "E122.1.0", {"start": v(3.5, -4.18) * mm, "end": v(2.99, -4) * mm});
            skLineSegment(sketch, "E122.2.0", {"start": v(4.3, -3.36) * mm, "end": v(3.76, -3.3) * mm});
            skLineSegment(sketch, "E122.3.0", {"start": v(4.9, -2.39) * mm, "end": v(4.36, -2.45) * mm});
            skLineSegment(sketch, "E122.4.0", {"start": v(5.29, -1.32) * mm, "end": v(4.77, -1.49) * mm});
            skLineSegment(sketch, "E122.5.0", {"start": v(5.45, -0.2) * mm, "end": v(4.98, -0.46) * mm});
            skLineSegment(sketch, "E122.6.0", {"start": v(5.37, 0.95) * mm, "end": v(4.97, 0.58) * mm});
            skLineSegment(sketch, "E122.7.0", {"start": v(5.05, 2.04) * mm, "end": v(4.74, 1.6) * mm});
            skLineSegment(sketch, "E122.8.0", {"start": v(4.52, 3.05) * mm, "end": v(4.3, 2.55) * mm});
            skLineSegment(sketch, "E122.9.0", {"start": v(3.79, 3.92) * mm, "end": v(3.67, 3.4) * mm});
            skLineSegment(sketch, "E122.10.0", {"start": v(2.89, 4.62) * mm, "end": v(2.89, 4.08) * mm});
            skLineSegment(sketch, "E122.11.0", {"start": v(1.86, 5.12) * mm, "end": v(1.98, 4.6) * mm});
            skLineSegment(sketch, "E122.12.0", {"start": v(0.76, 5.4) * mm, "end": v(0.98, 4.9) * mm});
            skLineSegment(sketch, "E122.13.0", {"start": v(-0.38, 5.44) * mm, "end": v(-0.06, 5) * mm});
            skLineSegment(sketch, "E122.14.0", {"start": v(-1.5, 5.24) * mm, "end": v(-1.1, 4.88) * mm});
            skLineSegment(sketch, "E122.15.0", {"start": v(-2.56, 4.81) * mm, "end": v(-2.1, 4.54) * mm});
            skLineSegment(sketch, "E122.16.0", {"start": v(-3.5, 4.18) * mm, "end": v(-2.99, 4) * mm});
            skLineSegment(sketch, "E122.17.0", {"start": v(-4.3, 3.36) * mm, "end": v(-3.76, 3.3) * mm});
            skLineSegment(sketch, "E122.18.0", {"start": v(-4.9, 2.39) * mm, "end": v(-4.36, 2.45) * mm});
            skLineSegment(sketch, "E122.19.0", {"start": v(-5.29, 1.32) * mm, "end": v(-4.77, 1.49) * mm});
            skLineSegment(sketch, "E122.20.0", {"start": v(-5.45, 0.2) * mm, "end": v(-4.98, 0.46) * mm});
            skLineSegment(sketch, "E122.21.0", {"start": v(-5.37, -0.95) * mm, "end": v(-4.97, -0.58) * mm});
            skLineSegment(sketch, "E122.22.0", {"start": v(-5.05, -2.04) * mm, "end": v(-4.74, -1.6) * mm});
            skLineSegment(sketch, "E122.23.0", {"start": v(-4.52, -3.05) * mm, "end": v(-4.3, -2.55) * mm});
            skLineSegment(sketch, "E122.24.0", {"start": v(-3.79, -3.92) * mm, "end": v(-3.67, -3.4) * mm});
            skLineSegment(sketch, "E122.25.0", {"start": v(-2.89, -4.62) * mm, "end": v(-2.89, -4.08) * mm});
            skLineSegment(sketch, "E122.26.0", {"start": v(-1.86, -5.12) * mm, "end": v(-1.98, -4.6) * mm});
            skLineSegment(sketch, "E122.27.0", {"start": v(-0.76, -5.4) * mm, "end": v(-0.98, -4.9) * mm});
            skLineSegment(sketch, "E122.28.0", {"start": v(0.38, -5.44) * mm, "end": v(0.06, -5) * mm});
            skLineSegment(sketch, "E122.29.0", {"start": v(1.5, -5.24) * mm, "end": v(1.1, -4.88) * mm});
            skPoint(sketch, "E123.orphan", {"position": v(4.28, 2.12) * mm});
            skPoint(sketch, "E124.orphan", {"position": v(4.2, 2.33) * mm});
            skSolve(sketch);
        }
        {
            var Q0;
            Q0 = qSketchRegion(id + "F52", true);
            extrude(context, id + "F53", {"entities" : qUnion([Q0]), "operationType" : NewBodyOperationType.ADD, "depth" : 4 * mm});
        }
        {
            var Q0;
            Q0=qCreatedBy(id+"F47.planeOp",FACE);
            cPlane(context, id + "F54", {"entities" : qUnion([Q0]), "cplaneType" : CPlaneType.OFFSET, "offset" : 8.5 * mm, "width" : 150 * mm, "height" : 150 * mm});
        }
        {
            var Q0;
            Q0=qCreatedBy(id+"F54.planeOp",FACE);
            var sketch = newSketch(context, id + "F55", { "sketchPlane" : qUnion([Q0])});
            skCircle(sketch, "E125", {"center": v(0, 0) * mm, "radius": 2 * mm});
            skSolve(sketch);
        }
        {
            var Q0;
            Q0=makeQuery(id+"F53.opExtrude","CAP_FACE",FACE,{"disambiguationData":[OSD([sQuery(id+"F52.wireOp",EDGE,"E118"),sQuery(id+"F52.wireOp",EDGE,"E119.0"),sQuery(id+"F52.wireOp",EDGE,"E119.1"),sQuery(id+"F52.wireOp",EDGE,"E120.1.0"),sQuery(id+"F52.wireOp",EDGE,"E120.2.0"),sQuery(id+"F52.wireOp",EDGE,"E121.2.3.0"),sQuery(id+"F52.wireOp",EDGE,"E121.2.4.0"),sQuery(id+"F52.wireOp",EDGE,"E121.2.5.0"),sQuery(id+"F52.wireOp",EDGE,"E121.2.6.0"),sQuery(id+"F52.wireOp",EDGE,"E121.2.7.0"),sQuery(id+"F52.wireOp",EDGE,"E121.2.8.0"),sQuery(id+"F52.wireOp",EDGE,"E121.2.9.0"),sQuery(id+"F52.wireOp",EDGE,"E121.2.10.0"),sQuery(id+"F52.wireOp",EDGE,"E121.2.11.0"),sQuery(id+"F52.wireOp",EDGE,"E121.2.12.0"),sQuery(id+"F52.wireOp",EDGE,"E121.2.13.0"),sQuery(id+"F52.wireOp",EDGE,"E121.2.14.0"),sQuery(id+"F52.wireOp",EDGE,"E121.2.15.0"),sQuery(id+"F52.wireOp",EDGE,"E121.2.16.0"),sQuery(id+"F52.wireOp",EDGE,"E121.2.17.0"),sQuery(id+"F52.wireOp",EDGE,"E121.2.18.0"),sQuery(id+"F52.wireOp",EDGE,"E121.2.19.0"),sQuery(id+"F52.wireOp",EDGE,"E121.2.20.0"),sQuery(id+"F52.wireOp",EDGE,"E121.2.21.0"),sQuery(id+"F52.wireOp",EDGE,"E121.2.22.0"),sQuery(id+"F52.wireOp",EDGE,"E121.2.23.0"),sQuery(id+"F52.wireOp",EDGE,"E121.2.24.0"),sQuery(id+"F52.wireOp",EDGE,"E121.2.25.0"),sQuery(id+"F52.wireOp",EDGE,"E121.2.26.0"),sQuery(id+"F52.wireOp",EDGE,"E121.2.27.0"),sQuery(id+"F52.wireOp",EDGE,"E121.2.28.0"),sQuery(id+"F52.wireOp",EDGE,"E121.2.29.0"),sQuery(id+"F52.wireOp",EDGE,"E122.1.0"),sQuery(id+"F52.wireOp",EDGE,"E122.2.0"),sQuery(id+"F52.wireOp",EDGE,"E122.3.0"),sQuery(id+"F52.wireOp",EDGE,"E122.4.0"),sQuery(id+"F52.wireOp",EDGE,"E122.5.0"),sQuery(id+"F52.wireOp",EDGE,"E122.6.0"),sQuery(id+"F52.wireOp",EDGE,"E122.7.0"),sQuery(id+"F52.wireOp",EDGE,"E122.8.0"),sQuery(id+"F52.wireOp",EDGE,"E122.9.0"),sQuery(id+"F52.wireOp",EDGE,"E122.10.0"),sQuery(id+"F52.wireOp",EDGE,"E122.11.0"),sQuery(id+"F52.wireOp",EDGE,"E122.12.0"),sQuery(id+"F52.wireOp",EDGE,"E122.13.0"),sQuery(id+"F52.wireOp",EDGE,"E122.14.0"),sQuery(id+"F52.wireOp",EDGE,"E122.15.0"),sQuery(id+"F52.wireOp",EDGE,"E122.16.0"),sQuery(id+"F52.wireOp",EDGE,"E122.17.0"),sQuery(id+"F52.wireOp",EDGE,"E122.18.0"),sQuery(id+"F52.wireOp",EDGE,"E122.19.0"),sQuery(id+"F52.wireOp",EDGE,"E122.20.0"),sQuery(id+"F52.wireOp",EDGE,"E122.21.0"),sQuery(id+"F52.wireOp",EDGE,"E122.22.0"),sQuery(id+"F52.wireOp",EDGE,"E122.23.0"),sQuery(id+"F52.wireOp",EDGE,"E122.24.0"),sQuery(id+"F52.wireOp",EDGE,"E122.25.0"),sQuery(id+"F52.wireOp",EDGE,"E122.26.0"),sQuery(id+"F52.wireOp",EDGE,"E122.27.0"),sQuery(id+"F52.wireOp",EDGE,"E122.28.0"),sQuery(id+"F52.wireOp",EDGE,"E122.29.0")])],"isStart":false});
            var sketch = newSketch(context, id + "F56", { "sketchPlane" : qUnion([Q0])});
            skCircle(sketch, "E126", {"center": v(0, 0) * mm, "radius": 5 * mm});
            skSolve(sketch);
        }
        {
            var Q1;
            {var subQ0=sQuery(id+"F56.wireOp",EDGE,"E126");var subQ44=makeQuery(id+"F56.imprint","INTERSECT",VERTEX,{"derivedFrom":[makeQuery(id+"F53.opExtrude","CAP_EDGE",EDGE,{"disambiguationData":[OSD([sQuery(id+"F52.wireOp",EDGE,"E121.2.5.0")])],"isStart":false}),subQ0]});Q1=makeQuery(id+"F56.imprint","IMPRINT",FACE,{"disambiguationData":[TD([[makeQuery(id+"F56.imprint","IMPRINT",EDGE,{"disambiguationData":[TD([[subQ44,-1.0]])],"derivedFrom":subQ0}),1.0]])]});}
            var Q2;
            Q2=makeQuery(id+"F55.imprint","IMPRINT",FACE,{"disambiguationData":[TD([[makeQuery(id+"F55.imprint","IMPRINT",EDGE,{"derivedFrom":sQuery(id+"F55.wireOp",EDGE,"E125")}),1.0]])]});
            loft(context, id + "F57", {"operationType" : NewBodyOperationType.ADD, "sheetProfilesArray" : [{ "sheetProfileEntities" : qUnion([Q1]) }, { "sheetProfileEntities" : qUnion([Q2]) }]});
        }
        {
            var Q0;
            Q0=makeQuery(id+"F57.opLoft","CAP_FACE",FACE,{"disambiguationData":[OSD([makeQuery(id+"F55.imprint","IMPRINT",FACE,{"disambiguationData":[TD([[makeQuery(id+"F55.imprint","IMPRINT",EDGE,{"derivedFrom":sQuery(id+"F55.wireOp",EDGE,"E125")}),1.0]])]})])],"isStart":true});
            var sketch = newSketch(context, id + "F58", { "sketchPlane" : qUnion([Q0])});
            skCircle(sketch, "E127", {"center": v(0, 0) * mm, "radius": 2 * mm});
            skSolve(sketch);
        }
        {
            var Q0;
            Q0 = qSketchRegion(id + "F58", true);
            extrude(context, id + "F59", {"entities" : qUnion([Q0]), "operationType" : NewBodyOperationType.ADD, "depth" : 5 * mm});
        }
        {
            var Q0;
            {var subQ0=sQuery(id+"F0.wireOp",EDGE,"E0.right");var subQ1=sQuery(id+"F0.wireOp",EDGE,"E0.bottom");Q0=makeQuery(id+"F3.boolean.opBoolean","SPLIT",FACE,{"disambiguationData":[TD([makeQuery(id+"F1.opExtrude","SWEPT_FACE",FACE,{"disambiguationData":[OSD([subQ0])]})])],"derivedFrom":makeQuery(id+"F1.opExtrude","CAP_FACE",FACE,{"disambiguationData":[OSD([subQ1,sQuery(id+"F0.wireOp",EDGE,"E0.top"),sQuery(id+"F0.wireOp",EDGE,"E0.left"),subQ0])],"isStart":false})});}
            var sketch = newSketch(context, id + "F60", { "sketchPlane" : qUnion([Q0])});
            skLineSegment(sketch, "E128", {"start": v(-16.43, 20.44) * mm, "end": v(-16.42, -4.94) * mm});
            skLineSegment(sketch, "E129", {"start": v(-17.93, 22.85) * mm, "end": v(-17.92, -7.35) * mm});
            skLineSegment(sketch, "E130", {"start": v(-19.93, 24.38) * mm, "end": v(-19.93, -8.88) * mm});
            skLineSegment(sketch, "E131", {"start": v(-23.3, 25.25) * mm, "end": v(-23.3, -9.75) * mm});
            skArc(sketch, "E132", {"start": v(-16.43, 20.44) * mm, "mid": v(-19.12, 23.91) * mm, "end": v(-23.3, 25.25) * mm});
            skPoint(sketch, "E132.third.point", {"position": v(-29.25, 13.33) * mm});
            skPoint(sketch, "E133", {"position": v(-15.93, 17.75) * mm});
            skArc(sketch, "E134", {"start": v(-15.93, 17.75) * mm, "mid": v(-16.05, 19.12) * mm, "end": v(-16.43, 20.44) * mm});
            skPoint(sketch, "E135.end.orphan", {"position": v(-21.42, -9.75) * mm});
            skLineSegment(sketch, "E136", {"start": v(-21.42, -9.48) * mm, "end": v(-21.42, 24.98) * mm});
            skPoint(sketch, "E137.first.point", {"position": v(-15.92, -2.25) * mm});
            skPoint(sketch, "E137.third.point", {"position": v(-28.91, 2.76) * mm});
            skArc(sketch, "E138.trimOffspring", {"start": v(-23.3, -9.75) * mm, "mid": v(-18.07, -7.52) * mm, "end": v(-15.92, -2.25) * mm});
            skLineSegment(sketch, "E139", {"start": v(-15.93, 17.75) * mm, "end": v(-15.92, -2.25) * mm});
            skSolve(sketch);
        }
        {
            var Q0;
            Q0=makeQuery(id+"F23.opExtrude","CAP_EDGE",EDGE,{"disambiguationData":[OSD([sQuery(id+"F22.wireOp",EDGE,"E68.left")])],"isStart":false});
            fillet(context, id + "F61", {"entities" : qUnion([Q0]), "radius" : 5 * mm, "tangentPropagation" : true, "allowEdgeOverflow" : false});
        }
        {
            var Q0;
            Q0=makeQuery(id+"F23.opExtrude","CAP_EDGE",EDGE,{"disambiguationData":[OSD([sQuery(id+"F22.wireOp",EDGE,"E68.left")])],"isStart":true});
            var Q1;
            Q1=makeQuery(id+"F23.opExtrude","CAP_EDGE",EDGE,{"disambiguationData":[OSD([sQuery(id+"F22.wireOp",EDGE,"E68.right")])],"isStart":true});
            var Q2;
            Q2=makeQuery(id+"F23.opExtrude","CAP_EDGE",EDGE,{"disambiguationData":[OSD([sQuery(id+"F22.wireOp",EDGE,"E68.right")])],"isStart":false});
            var Q3;
            Q3=makeQuery(id+"F19.opExtrude","CAP_EDGE",EDGE,{"disambiguationData":[OSD([sQuery(id+"F18.wireOp",EDGE,"E63")])],"isStart":false});
            var Q4;
            Q4=makeQuery(id+"F19.opExtrude","CAP_EDGE",EDGE,{"disambiguationData":[OSD([sQuery(id+"F18.wireOp",EDGE,"E61")])],"isStart":false});
            var Q5;
            Q5=makeQuery(id+"F17.opExtrude","CAP_EDGE",EDGE,{"disambiguationData":[OSD([sQuery(id+"F16.wireOp",EDGE,"E59")])],"isStart":false});
            var Q6;
            Q6=makeQuery(id+"F15.opExtrude","CAP_EDGE",EDGE,{"disambiguationData":[OSD([sQuery(id+"F14.wireOp",EDGE,"E54")])],"isStart":false});
            fillet(context, id + "F62", {"entities" : qUnion([Q0, Q1, Q2, Q3, Q4, Q5, Q6]), "radius" : 5 * mm, "tangentPropagation" : true, "allowEdgeOverflow" : false});
        }
        {
            var Q0;
            {var subQ5=sQuery(id+"F60.wireOp",EDGE,"E136");Q0=makeQuery(id+"F60.imprint","IMPRINT",FACE,{"disambiguationData":[TD([[makeQuery(id+"F60.imprint","IMPRINT",EDGE,{"derivedFrom":subQ5}),1.0]])]});}
            extrude(context, id + "F63", {"entities" : qUnion([Q0]), "operationType" : NewBodyOperationType.REMOVE, "oppositeDirection" : true, "depth" : 2 * mm});
        }
        {
            var Q0;
            {var subQ0=sQuery(id+"F60.wireOp",EDGE,"E129");Q0=makeQuery(id+"F60.imprint","IMPRINT",FACE,{"disambiguationData":[TD([[makeQuery(id+"F60.imprint","IMPRINT",EDGE,{"derivedFrom":subQ0}),-1.0]])]});}
            var Q1;
            {var subQ0=sQuery(id+"F60.wireOp",EDGE,"E128");Q1=makeQuery(id+"F60.imprint","IMPRINT",FACE,{"disambiguationData":[TD([[makeQuery(id+"F60.imprint","IMPRINT",EDGE,{"derivedFrom":subQ0}),1.0]])]});}
            extrude(context, id + "F64", {"entities" : qUnion([Q0, Q1]), "operationType" : NewBodyOperationType.REMOVE, "oppositeDirection" : true, "depth" : 2 * mm});
        }
        {
            var Q0;
            Q0=makeQuery(id+"F1.opExtrude","CAP_EDGE",EDGE,{"disambiguationData":[OSD([sQuery(id+"F0.wireOp",EDGE,"E0.right")])],"isStart":false});
            fillet(context, id + "F65", {"entities" : qUnion([Q0]), "radius" : 5 * mm, "tangentPropagation" : true, "allowEdgeOverflow" : false});
        }
        {
            var Q0;
            {var subQ0=sQuery(id+"F0.wireOp",EDGE,"E0.left");var subQ1=sQuery(id+"F0.wireOp",EDGE,"E0.bottom");Q0=makeQuery(id+"F3.boolean.opBoolean","SPLIT",FACE,{"disambiguationData":[TD([makeQuery(id+"F1.opExtrude","SWEPT_FACE",FACE,{"disambiguationData":[OSD([subQ0])]})])],"derivedFrom":makeQuery(id+"F1.opExtrude","CAP_FACE",FACE,{"disambiguationData":[OSD([subQ1,sQuery(id+"F0.wireOp",EDGE,"E0.top"),subQ0,sQuery(id+"F0.wireOp",EDGE,"E0.right")])],"isStart":false})});}
            var sketch = newSketch(context, id + "F66", { "sketchPlane" : qUnion([Q0])});
            skLineSegment(sketch, "E140", {"start": v(16.42, 20.44) * mm, "end": v(16.42, -4.94) * mm});
            skLineSegment(sketch, "E141", {"start": v(17.92, 22.85) * mm, "end": v(17.93, -7.35) * mm});
            skLineSegment(sketch, "E142", {"start": v(17.93, -7.35) * mm, "end": v(17.9, -7) * mm});
            skLineSegment(sketch, "E143", {"start": v(19.92, 24.38) * mm, "end": v(19.93, -8.88) * mm});
            skLineSegment(sketch, "E144", {"start": v(21.42, 24.98) * mm, "end": v(21.43, -9.48) * mm});
            skPoint(sketch, "E145.endSnap0", {"position": v(27.98, -9.75) * mm});
            skPoint(sketch, "E146.first.point", {"position": v(15.92, 17.75) * mm});
            skPoint(sketch, "E146.third.point", {"position": v(30.03, 14.4) * mm});
            skPoint(sketch, "E147.first.point", {"position": v(15.92, -2.25) * mm});
            skPoint(sketch, "E147.third.point", {"position": v(29.77, 3.26) * mm});
            skLineSegment(sketch, "E148", {"start": v(15.92, 17.75) * mm, "end": v(15.92, -2.25) * mm});
            skArc(sketch, "E149", {"start": v(21.42, 24.98) * mm, "mid": v(17.46, 22.3) * mm, "end": v(15.92, 17.75) * mm});
            skArc(sketch, "E150", {"start": v(15.92, -2.25) * mm, "mid": v(17.46, -6.8) * mm, "end": v(21.43, -9.48) * mm});
            skPoint(sketch, "E151.orphan", {"position": v(23.43, -9.75) * mm});
            skLineSegment(sketch, "E152", {"start": v(23.42, 25.25) * mm, "end": v(23.43, -9.75) * mm});
            skArc(sketch, "E153", {"start": v(23.42, 25.25) * mm, "mid": v(18.12, 23.05) * mm, "end": v(15.92, 17.75) * mm});
            skArc(sketch, "E154", {"start": v(15.92, -2.25) * mm, "mid": v(18.12, -7.55) * mm, "end": v(23.43, -9.75) * mm});
            skLineSegment(sketch, "E155", {"start": v(21.42, 24.98) * mm, "end": v(23.42, 24.98) * mm});
            skLineSegment(sketch, "E156", {"start": v(21.43, -9.48) * mm, "end": v(23.43, -9.48) * mm});
            skSolve(sketch);
        }
        {
            var Q0;
            {var subQ6=sQuery(id+"F66.wireOp",EDGE,"E143");Q0=makeQuery(id+"F66.imprint","IMPRINT",FACE,{"disambiguationData":[TD([[makeQuery(id+"F66.imprint","IMPRINT",EDGE,{"derivedFrom":subQ6}),-1.0]])]});}
            var Q1;
            {var subQ3=sQuery(id+"F66.wireOp",EDGE,"E140");Q1=makeQuery(id+"F66.imprint","IMPRINT",FACE,{"disambiguationData":[TD([[makeQuery(id+"F66.imprint","IMPRINT",EDGE,{"derivedFrom":subQ3}),-1.0]])]});}
            extrude(context, id + "F67", {"entities" : qUnion([Q0, Q1]), "operationType" : NewBodyOperationType.REMOVE, "oppositeDirection" : true, "depth" : 2 * mm});
        }
        {
            var Q0;
            Q0=makeQuery(id+"F1.opExtrude","CAP_EDGE",EDGE,{"disambiguationData":[OSD([sQuery(id+"F0.wireOp",EDGE,"E0.left")])],"isStart":false});
            fillet(context, id + "F68", {"entities" : qUnion([Q0]), "radius" : 5 * mm, "tangentPropagation" : true, "allowEdgeOverflow" : false});
        }
        {
            var Q0;
            Q0=makeQuery(id+"F66.imprint","IMPRINT",FACE,{"disambiguationData":[TD([[makeQuery(id+"F66.imprint","IMPRINT",EDGE,{"derivedFrom":sQuery(id+"F66.wireOp",EDGE,"E144")}),1.0]])]});
            extrude(context, id + "F69", {"entities" : qUnion([Q0]), "operationType" : NewBodyOperationType.REMOVE, "oppositeDirection" : true, "depth" : 2 * mm});
        }
        {
            var Q0;
            {var subQ3=sQuery(id+"F66.wireOp",EDGE,"E156");Q0=makeQuery(id+"F66.imprint","IMPRINT",FACE,{"disambiguationData":[TD([[makeQuery(id+"F66.imprint","IMPRINT",EDGE,{"derivedFrom":subQ3}),-1.0]])]});}
            extrude(context, id + "F70", {"entities" : qUnion([Q0]), "operationType" : NewBodyOperationType.REMOVE, "oppositeDirection" : true, "depth" : 2 * mm});
        }
        {
            var Q0;
            Q0=makeQuery(id+"F6.boolean.opBoolean","MERGE",EDGE,{"derivedFrom":[makeQuery(id+"F1.opExtrude","CAP_EDGE",EDGE,{"disambiguationData":[OSD([sQuery(id+"F0.wireOp",EDGE,"E0.right")])],"isStart":true}),makeQuery(id+"F6.opExtrude","SWEPT_EDGE",EDGE,{"disambiguationData":[OSD([sQuery(id+"F5.wireOp",EDGE,"E31.top"),sQuery(id+"F5.wireOp",EDGE,"E31.left")])]})]});
            fillet(context, id + "F71", {"entities" : qUnion([Q0]), "radius" : 5 * mm, "tangentPropagation" : true, "allowEdgeOverflow" : false});
        }
        {
            var Q0;
            Q0=makeQuery(id+"F6.boolean.opBoolean","MERGE",EDGE,{"derivedFrom":[makeQuery(id+"F1.opExtrude","CAP_EDGE",EDGE,{"disambiguationData":[OSD([sQuery(id+"F0.wireOp",EDGE,"E0.left")])],"isStart":true}),makeQuery(id+"F6.opExtrude","SWEPT_EDGE",EDGE,{"disambiguationData":[OSD([sQuery(id+"F5.wireOp",EDGE,"E31.top"),sQuery(id+"F5.wireOp",EDGE,"E31.right")])]})]});
            fillet(context, id + "F72", {"entities" : qUnion([Q0]), "radius" : 5 * mm, "tangentPropagation" : true, "allowEdgeOverflow" : false});
        }
        {
            var Q0;
            Q0=makeQuery(id+"F6.boolean.opBoolean","MERGE",FACE,{"derivedFrom":[makeQuery(id+"F3.boolean.opBoolean","MERGE",FACE,{"derivedFrom":[makeQuery(id+"F1.opExtrude","SWEPT_FACE",FACE,{"disambiguationData":[OSD([sQuery(id+"F0.wireOp",EDGE,"E0.right")])]}),makeQuery(id+"F3.opExtrude","SWEPT_FACE",FACE,{"disambiguationData":[OSD([sQuery(id+"F2.wireOp",EDGE,"E5")])]})]}),makeQuery(id+"F6.opExtrude","SWEPT_FACE",FACE,{"disambiguationData":[OSD([sQuery(id+"F5.wireOp",EDGE,"E31.left")])]})]});
            var sketch = newSketch(context, id + "F73", { "sketchPlane" : qUnion([Q0])});
            skLineSegment(sketch, "E157", {"start": v(7, 25.25) * mm, "end": v(7, -9.75) * mm});
            skLineSegment(sketch, "E158", {"start": v(5, 25.25) * mm, "end": v(5, -9.75) * mm});
            skLineSegment(sketch, "E159", {"start": v(3.5, 25.25) * mm, "end": v(3.5, -9.75) * mm});
            skLineSegment(sketch, "E160", {"start": v(8.5, 25.25) * mm, "end": v(8.5, -9.75) * mm});
            skLineSegment(sketch, "E161", {"start": v(1.5, 25.25) * mm, "end": v(1.5, -9.75) * mm});
            skLineSegment(sketch, "E162", {"start": v(0, 25.25) * mm, "end": v(0, -9.75) * mm});
            skLineSegment(sketch, "E163", {"start": v(-2, 25.25) * mm, "end": v(-2, -9.75) * mm});
            skLineSegment(sketch, "E164", {"start": v(-3.5, 25.25) * mm, "end": v(-3.5, -9.75) * mm});
            skLineSegment(sketch, "E165", {"start": v(-5.5, 25.25) * mm, "end": v(-5.5, -9.75) * mm});
            skLineSegment(sketch, "E166", {"start": v(-7, 25.25) * mm, "end": v(-7, -9.75) * mm});
            skLineSegment(sketch, "E167", {"start": v(-9, 25.25) * mm, "end": v(-9, -9.75) * mm});
            skLineSegment(sketch, "E168", {"start": v(-10.5, 25.25) * mm, "end": v(-10.5, -9.75) * mm});
            skLineSegment(sketch, "E169", {"start": v(-10.5, 25.25) * mm, "end": v(8.5, 25.25) * mm});
            skLineSegment(sketch, "E170", {"start": v(-10.5, -9.75) * mm, "end": v(10.5, -9.75) * mm});
            skLineSegment(sketch, "E171", {"start": v(10.5, -9.75) * mm, "end": v(10.5, 25.25) * mm});
            skLineSegment(sketch, "E172", {"start": v(10.5, 25.25) * mm, "end": v(8.5, 25.25) * mm});
            skSolve(sketch);
        }
        {
            var Q0;
            {var subQ0=sQuery(id+"F73.wireOp",EDGE,"E166");Q0=makeQuery(id+"F73.imprint","IMPRINT",FACE,{"disambiguationData":[TD([[makeQuery(id+"F73.imprint","IMPRINT",EDGE,{"derivedFrom":subQ0}),-1.0]])]});}
            var Q1;
            {var subQ0=sQuery(id+"F73.wireOp",EDGE,"E164");Q1=makeQuery(id+"F73.imprint","IMPRINT",FACE,{"disambiguationData":[TD([[makeQuery(id+"F73.imprint","IMPRINT",EDGE,{"derivedFrom":subQ0}),-1.0]])]});}
            var Q2;
            {var subQ0=sQuery(id+"F73.wireOp",EDGE,"E162");Q2=makeQuery(id+"F73.imprint","IMPRINT",FACE,{"disambiguationData":[TD([[makeQuery(id+"F73.imprint","IMPRINT",EDGE,{"derivedFrom":subQ0}),-1.0]])]});}
            var Q3;
            {var subQ0=sQuery(id+"F73.wireOp",EDGE,"E159");Q3=makeQuery(id+"F73.imprint","IMPRINT",FACE,{"disambiguationData":[TD([[makeQuery(id+"F73.imprint","IMPRINT",EDGE,{"derivedFrom":subQ0}),-1.0]])]});}
            var Q4;
            {var subQ0=sQuery(id+"F73.wireOp",EDGE,"E157");Q4=makeQuery(id+"F73.imprint","IMPRINT",FACE,{"disambiguationData":[TD([[makeQuery(id+"F73.imprint","IMPRINT",EDGE,{"derivedFrom":subQ0}),-1.0]])]});}
            var Q5;
            {var subQ0=sQuery(id+"F73.wireOp",EDGE,"E160");Q5=makeQuery(id+"F73.imprint","IMPRINT",FACE,{"disambiguationData":[TD([[makeQuery(id+"F73.imprint","IMPRINT",EDGE,{"derivedFrom":subQ0}),1.0]])]});}
            extrude(context, id + "F74", {"entities" : qUnion([Q0, Q1, Q2, Q3, Q4, Q5]), "operationType" : NewBodyOperationType.REMOVE, "oppositeDirection" : true, "depth" : 2 * mm});
        }
        {
            var Q0;
            Q0=makeQuery(id+"F6.boolean.opBoolean","MERGE",FACE,{"derivedFrom":[makeQuery(id+"F3.boolean.opBoolean","MERGE",FACE,{"derivedFrom":[makeQuery(id+"F1.opExtrude","SWEPT_FACE",FACE,{"disambiguationData":[OSD([sQuery(id+"F0.wireOp",EDGE,"E0.left")])]}),makeQuery(id+"F3.opExtrude","SWEPT_FACE",FACE,{"disambiguationData":[OSD([sQuery(id+"F2.wireOp",EDGE,"E6")])]})]}),makeQuery(id+"F6.opExtrude","SWEPT_FACE",FACE,{"disambiguationData":[OSD([sQuery(id+"F5.wireOp",EDGE,"E31.right")])]})]});
            var sketch = newSketch(context, id + "F75", { "sketchPlane" : qUnion([Q0])});
            skLineSegment(sketch, "E173", {"start": v(-10.5, 25.25) * mm, "end": v(-10.5, -9.75) * mm});
            skLineSegment(sketch, "E174", {"start": v(-10.5, -9.75) * mm, "end": v(10.5, -9.75) * mm});
            skLineSegment(sketch, "E175", {"start": v(10.5, -9.75) * mm, "end": v(10.5, 25.25) * mm});
            skLineSegment(sketch, "E176", {"start": v(10.5, 25.25) * mm, "end": v(-10.5, 25.25) * mm});
            skLineSegment(sketch, "E177", {"start": v(-8.5, 25.25) * mm, "end": v(-8.5, -9.75) * mm});
            skLineSegment(sketch, "E178", {"start": v(-7, 25.25) * mm, "end": v(-7, -9.75) * mm});
            skLineSegment(sketch, "E179", {"start": v(-5, 25.25) * mm, "end": v(-5, -9.75) * mm});
            skLineSegment(sketch, "E180", {"start": v(-3.5, 25.25) * mm, "end": v(-3.5, -9.75) * mm});
            skLineSegment(sketch, "E181", {"start": v(-1.5, 25.25) * mm, "end": v(-1.5, -9.75) * mm});
            skLineSegment(sketch, "E182", {"start": v(0, 25.25) * mm, "end": v(0, -9.75) * mm});
            skLineSegment(sketch, "E183", {"start": v(2, 25.25) * mm, "end": v(2, -9.75) * mm});
            skLineSegment(sketch, "E184", {"start": v(3.5, 25.25) * mm, "end": v(3.5, -9.75) * mm});
            skLineSegment(sketch, "E185", {"start": v(5.5, 25.25) * mm, "end": v(5.5, -9.75) * mm});
            skLineSegment(sketch, "E186", {"start": v(9, 25.25) * mm, "end": v(9, -9.75) * mm});
            skLineSegment(sketch, "E187", {"start": v(7, 25.25) * mm, "end": v(7, -9.75) * mm});
            skSolve(sketch);
        }
        {
            var Q0;
            {var subQ0=sQuery(id+"F75.wireOp",EDGE,"E173");Q0=makeQuery(id+"F75.imprint","IMPRINT",FACE,{"disambiguationData":[TD([[makeQuery(id+"F75.imprint","IMPRINT",EDGE,{"derivedFrom":subQ0}),1.0]])]});}
            var Q1;
            {var subQ0=sQuery(id+"F75.wireOp",EDGE,"E178");Q1=makeQuery(id+"F75.imprint","IMPRINT",FACE,{"disambiguationData":[TD([[makeQuery(id+"F75.imprint","IMPRINT",EDGE,{"derivedFrom":subQ0}),1.0]])]});}
            var Q2;
            {var subQ0=sQuery(id+"F75.wireOp",EDGE,"E180");Q2=makeQuery(id+"F75.imprint","IMPRINT",FACE,{"disambiguationData":[TD([[makeQuery(id+"F75.imprint","IMPRINT",EDGE,{"derivedFrom":subQ0}),1.0]])]});}
            var Q3;
            {var subQ0=sQuery(id+"F75.wireOp",EDGE,"E182");Q3=makeQuery(id+"F75.imprint","IMPRINT",FACE,{"disambiguationData":[TD([[makeQuery(id+"F75.imprint","IMPRINT",EDGE,{"derivedFrom":subQ0}),1.0]])]});}
            var Q4;
            {var subQ0=sQuery(id+"F75.wireOp",EDGE,"E184");Q4=makeQuery(id+"F75.imprint","IMPRINT",FACE,{"disambiguationData":[TD([[makeQuery(id+"F75.imprint","IMPRINT",EDGE,{"derivedFrom":subQ0}),1.0]])]});}
            var Q5;
            {var subQ0=sQuery(id+"F75.wireOp",EDGE,"E186");Q5=makeQuery(id+"F75.imprint","IMPRINT",FACE,{"disambiguationData":[TD([[makeQuery(id+"F75.imprint","IMPRINT",EDGE,{"derivedFrom":subQ0}),-1.0]])]});}
            extrude(context, id + "F76", {"entities" : qUnion([Q0, Q1, Q2, Q3, Q4, Q5]), "operationType" : NewBodyOperationType.REMOVE, "oppositeDirection" : true, "depth" : 2 * mm});
        }
    });
